# Revit family: AV-04AFD
name_source: partatom
category: Устройства связи
units: mm (PartAtom-declared; Revit-internal decimal feet)

## family parameters
Всегда вертикально = Нет
На основе рабочей плоскости = Да
Общий = Да
При загрузке вырезать с полостями = Нет
Размер круглого соединителя = Использовать диаметр
Сохранять ориентацию аннотаций = Нет
Тип детали = Нормальный
Точка принадлежности помещению = Нет

## types (1)
- AV-04AFD
    ADSK_URL документации изделия = https://www.bas-ip.ru
    ADSK_URL страницы изделия = https://www.bas-ip.ru
    ADSK_Версия Revit = Revit 2020
    ADSK_Единица измерения = шт
    ADSK_Завод-изготовитель = BAS-IP
    ADSK_Классификация нагрузок = Вызывная панель
    ADSK_Количество фаз = 1
    ADSK_Коэффициент мощности = 0.9
    ADSK_Марка = AV-04AFD
    ADSK_Наименование = ВЫЗЫВНАЯ ПАНЕЛЬ AV-04AFD
    ADSK_Наименование краткое = AV-04AFD
    ADSK_Напряжение = 12 В
    ADSK_Номинальная мощность = 7 Вт
    ADSK_Полная мощность = 7 В·А
    ADSK_Размер_Длина = 190 мм
    ADSK_Размер_Толщина = 27 мм
    ADSK_Размер_Ширина = 95 мм
    BIM library = https://bimlib.ru
    URL = https://www.bas-ip.ru
    Аутентификация = WEB–интерфейс
    Группа модели = Вызывная панель
    Дисплей = Нет
    Дополнительно = SIP P2P,  открытое API
    Изготовитель = BAS-IP
    Изображение типоразмера = <Нет>
    Интерфейс = WEB–интерфейс
    Класс степени защиты = IP65
    Кнопки быстрого вызова = Механическая кнопка
    Количество мелодий вызова = Установленные мелодии
    Корпус = Металл
    Материал корпуса = Материал темно-зеленый
    Описание = BAS-IP AV-04AFD - Эта панель может быть установлена на специальных объектах с повышенными требованиями к пожарной безопасности. Она помогает организовать обратную связь с диспетчерской для подтверждения пожарной или аварийной ситуации.
    Отметка по умолчанию = 0 мм
    Питание = + 12 Вольт, PoE
    Потребление питания = 6,5 Вт, в режиме ожидания – 2,5 Вт
    Размер панели = 95х190х27 мм
    Размер под установку, размер врезного кронштейна = 85х180х45 мм
    Режим разговора = Двухсторонний
    Температурный режим = -40 ... +65 °С
    Тип панели = Индивидуальная
    Тип установки = Врезной
    Цветовое решение = Серебро, Красный, Зеленый
